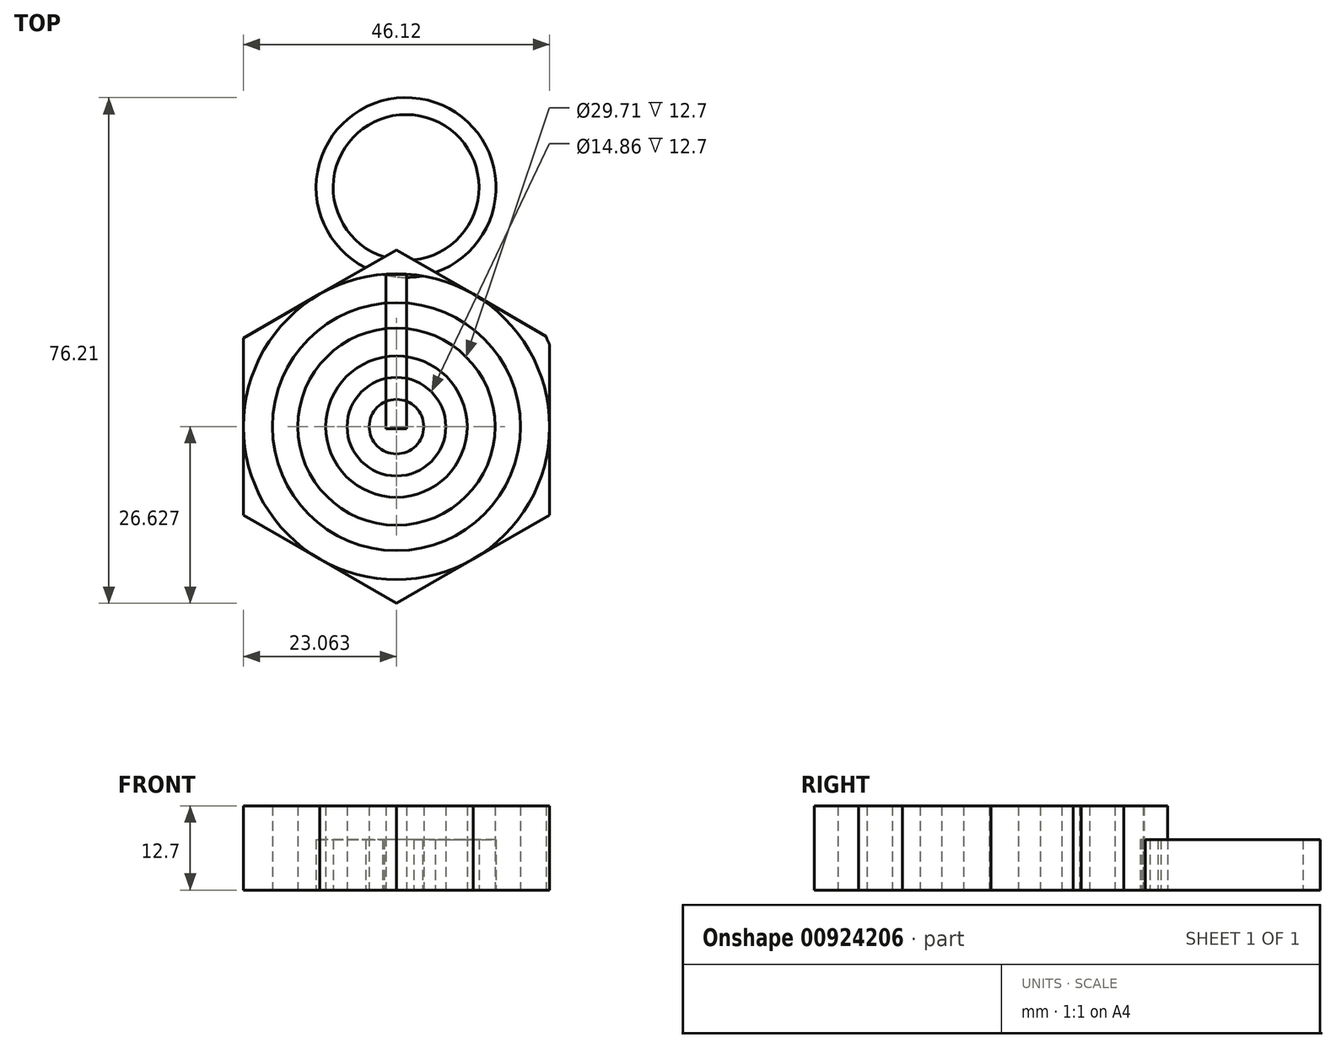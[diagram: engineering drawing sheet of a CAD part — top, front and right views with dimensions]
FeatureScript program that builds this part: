
annotation { "Feature Type Name" : "Feature", "Feature Type Description" : "" }
export const myFeature = defineFeature(function(context is Context, id is Id, definition is map)
    precondition{}
    {
        {
            var Q0;
            Q0=qCreatedBy(makeId("Top.planeOp"),FACE);
            var sketch = newSketch(context, id + "F0", { "sketchPlane" : qUnion([Q0])});
            skCircle(sketch, "E0", {"center": v(-116.2, 74.4) * mm, "radius": 9.94 * mm});
            skCircle(sketch, "E1", {"center": v(-116.2, 74.4) * mm, "radius": 8.77 * mm});
            skFitSpline(sketch, "E2", {"points": [v(-120.64, 65.51) * mm, v(-128.44, 54.58) * mm, v(-111.87, 23.6) * mm, v(-133.85, 25.04) * mm, v(-133.13, 26.12) * mm], "startDerivative": vector(-58.47, -33.46) * mm, "endDerivative": vector(22.26, 13.19) * mm});
            skCircle(sketch, "E3", {"center": v(-138.9, 24.32) * mm, "radius": 5.42 * mm});
            skCircle(sketch, "E4", {"center": v(-138.9, 24.32) * mm, "radius": 5.1 * mm});
            skCircle(sketch, "E5.cCircle", {"center": v(-166.64, 9.19) * mm, "radius": 23.06 * mm, "construction": true});
            skLineSegment(sketch, "E5.0", {"start": v(-143.58, 22.5) * mm, "end": v(-143.58, -4.13) * mm});
            skLineSegment(sketch, "E5.1", {"start": v(-143.58, -4.13) * mm, "end": v(-166.64, -17.44) * mm});
            skLineSegment(sketch, "E5.2", {"start": v(-166.64, -17.44) * mm, "end": v(-189.7, -4.13) * mm});
            skLineSegment(sketch, "E5.3", {"start": v(-189.7, -4.13) * mm, "end": v(-189.7, 22.5) * mm});
            skLineSegment(sketch, "E5.4", {"start": v(-189.7, 22.5) * mm, "end": v(-166.64, 35.81) * mm});
            skLineSegment(sketch, "E5.5", {"start": v(-166.64, 35.81) * mm, "end": v(-143.58, 22.5) * mm});
            skPoint(sketch, "E5.0.midPoint", {"position": v(-143.58, 9.19) * mm});
            skCircle(sketch, "E6", {"center": v(-166.64, 9.19) * mm, "radius": 23.06 * mm});
            skCircle(sketch, "E7", {"center": v(-166.64, 9.19) * mm, "radius": 18.69 * mm});
            skCircle(sketch, "E8", {"center": v(-166.64, 9.19) * mm, "radius": 14.86 * mm});
            skCircle(sketch, "E9", {"center": v(-166.64, 9.19) * mm, "radius": 10.65 * mm});
            skCircle(sketch, "E10", {"center": v(-166.64, 9.19) * mm, "radius": 7.43 * mm});
            skCircle(sketch, "E11", {"center": v(-166.64, 9.19) * mm, "radius": 4.1 * mm});
            skSolve(sketch);
        }
        {
            var Q0;
            {var subQ0=sQuery(id+"F0.wireOp",EDGE,"E5.5");var subQ1=sQuery(id+"F0.wireOp",EDGE,"E5.4");var subQ2=makeQuery(id+"F0.imprint","INTERSECT",VERTEX,{"derivedFrom":[subQ1,subQ0]});Q0=makeQuery(id+"F0.imprint","IMPRINT",FACE,{"disambiguationData":[TD([[makeQuery(id+"F0.imprint","IMPRINT",EDGE,{"disambiguationData":[TD([[subQ2,1.0]])],"derivedFrom":subQ1}),-1.0]])]});}
            var Q1;
            {var subQ0=sQuery(id+"F0.wireOp",EDGE,"E5.4");var subQ1=sQuery(id+"F0.wireOp",EDGE,"E5.3");var subQ2=makeQuery(id+"F0.imprint","INTERSECT",VERTEX,{"derivedFrom":[subQ1,subQ0]});Q1=makeQuery(id+"F0.imprint","IMPRINT",FACE,{"disambiguationData":[TD([[makeQuery(id+"F0.imprint","IMPRINT",EDGE,{"disambiguationData":[TD([[subQ2,1.0]])],"derivedFrom":subQ1}),-1.0]])]});}
            var Q2;
            {var subQ0=sQuery(id+"F0.wireOp",EDGE,"E5.3");var subQ1=sQuery(id+"F0.wireOp",EDGE,"E5.2");var subQ2=makeQuery(id+"F0.imprint","INTERSECT",VERTEX,{"derivedFrom":[subQ1,subQ0]});Q2=makeQuery(id+"F0.imprint","IMPRINT",FACE,{"disambiguationData":[TD([[makeQuery(id+"F0.imprint","IMPRINT",EDGE,{"disambiguationData":[TD([[subQ2,1.0]])],"derivedFrom":subQ1}),-1.0]])]});}
            var Q3;
            {var subQ0=sQuery(id+"F0.wireOp",EDGE,"E5.2");var subQ1=sQuery(id+"F0.wireOp",EDGE,"E5.1");var subQ2=makeQuery(id+"F0.imprint","INTERSECT",VERTEX,{"derivedFrom":[subQ1,subQ0]});Q3=makeQuery(id+"F0.imprint","IMPRINT",FACE,{"disambiguationData":[TD([[makeQuery(id+"F0.imprint","IMPRINT",EDGE,{"disambiguationData":[TD([[subQ2,1.0]])],"derivedFrom":subQ1}),-1.0]])]});}
            var Q4;
            {var subQ0=sQuery(id+"F0.wireOp",EDGE,"E5.1");var subQ1=sQuery(id+"F0.wireOp",EDGE,"E5.0");var subQ2=makeQuery(id+"F0.imprint","INTERSECT",VERTEX,{"derivedFrom":[subQ1,subQ0]});Q4=makeQuery(id+"F0.imprint","IMPRINT",FACE,{"disambiguationData":[TD([[makeQuery(id+"F0.imprint","IMPRINT",EDGE,{"disambiguationData":[TD([[subQ2,1.0]])],"derivedFrom":subQ1}),-1.0]])]});}
            var Q5;
            {var subQ0=sQuery(id+"F0.wireOp",EDGE,"E5.5");var subQ1=sQuery(id+"F0.wireOp",EDGE,"E3");var subQ2=makeQuery(id+"F0.imprint","INTERSECT",VERTEX,{"derivedFrom":[subQ1,subQ0]});Q5=makeQuery(id+"F0.imprint","IMPRINT",FACE,{"disambiguationData":[TD([[makeQuery(id+"F0.imprint","IMPRINT",EDGE,{"disambiguationData":[TD([[subQ2,-1.0]])],"derivedFrom":subQ1}),-1.0]])]});}
            var Q6;
            Q6=makeQuery(id+"F0.imprint","IMPRINT",FACE,{"disambiguationData":[TD([[makeQuery(id+"F0.imprint","IMPRINT",EDGE,{"derivedFrom":sQuery(id+"F0.wireOp",EDGE,"E7")}),1.0]])]});
            var Q7;
            Q7=makeQuery(id+"F0.imprint","IMPRINT",FACE,{"disambiguationData":[TD([[makeQuery(id+"F0.imprint","IMPRINT",EDGE,{"derivedFrom":sQuery(id+"F0.wireOp",EDGE,"E9")}),1.0]])]});
            var Q8;
            Q8=makeQuery(id+"F0.imprint","IMPRINT",FACE,{"disambiguationData":[TD([[makeQuery(id+"F0.imprint","IMPRINT",EDGE,{"derivedFrom":sQuery(id+"F0.wireOp",EDGE,"E11")}),1.0]])]});
            extrude(context, id + "F1", {"entities" : qUnion([Q0, Q1, Q2, Q3, Q4, Q5, Q6, Q7, Q8]), "depth" : 12.7 * mm, "offsetDistance" : 25.4 * mm});
        }
        {
            var Q0;
            Q0=qCreatedBy(makeId("Top.planeOp"),FACE);
            var sketch = newSketch(context, id + "F2", { "sketchPlane" : qUnion([Q0])});
            skCircle(sketch, "E12", {"center": v(-165.19, 45.22) * mm, "radius": 13.55 * mm});
            skCircle(sketch, "E13", {"center": v(-165.19, 45.22) * mm, "radius": 10.98 * mm});
            skSolve(sketch);
        }
        {
            var Q0;
            Q0=makeQuery(id+"F2.imprint","IMPRINT",FACE,{"disambiguationData":[TD([[makeQuery(id+"F2.imprint","IMPRINT",EDGE,{"derivedFrom":sQuery(id+"F2.wireOp",EDGE,"E12")}),1.0]])]});
            extrude(context, id + "F3", {"entities" : qUnion([Q0]), "operationType" : NewBodyOperationType.ADD, "depth" : 7.62 * mm, "offsetDistance" : 25.4 * mm});
        }
        {
            var Q0;
            Q0=qCreatedBy(makeId("Top.planeOp"),FACE);
            var sketch = newSketch(context, id + "F4", { "sketchPlane" : qUnion([Q0])});
            skLineSegment(sketch, "E14.bottom", {"start": v(-165.1, 32.12) * mm, "end": v(-168.2, 32.12) * mm});
            skLineSegment(sketch, "E14.top", {"start": v(-165.1, 8.9) * mm, "end": v(-168.2, 8.9) * mm});
            skLineSegment(sketch, "E14.left", {"start": v(-165.1, 32.12) * mm, "end": v(-165.1, 8.9) * mm});
            skLineSegment(sketch, "E14.right", {"start": v(-168.2, 32.12) * mm, "end": v(-168.2, 8.9) * mm});
            skSolve(sketch);
        }
        {
            var Q0;
            Q0=makeQuery(id+"F4.imprint","IMPRINT",FACE,{"disambiguationData":[TD([[makeQuery(id+"F4.imprint","IMPRINT",EDGE,{"derivedFrom":sQuery(id+"F4.wireOp",EDGE,"E14.bottom")}),1.0]])]});
            extrude(context, id + "F5", {"entities" : qUnion([Q0]), "depth" : 12.7 * mm, "offsetDistance" : 25.4 * mm});
        }
    });
